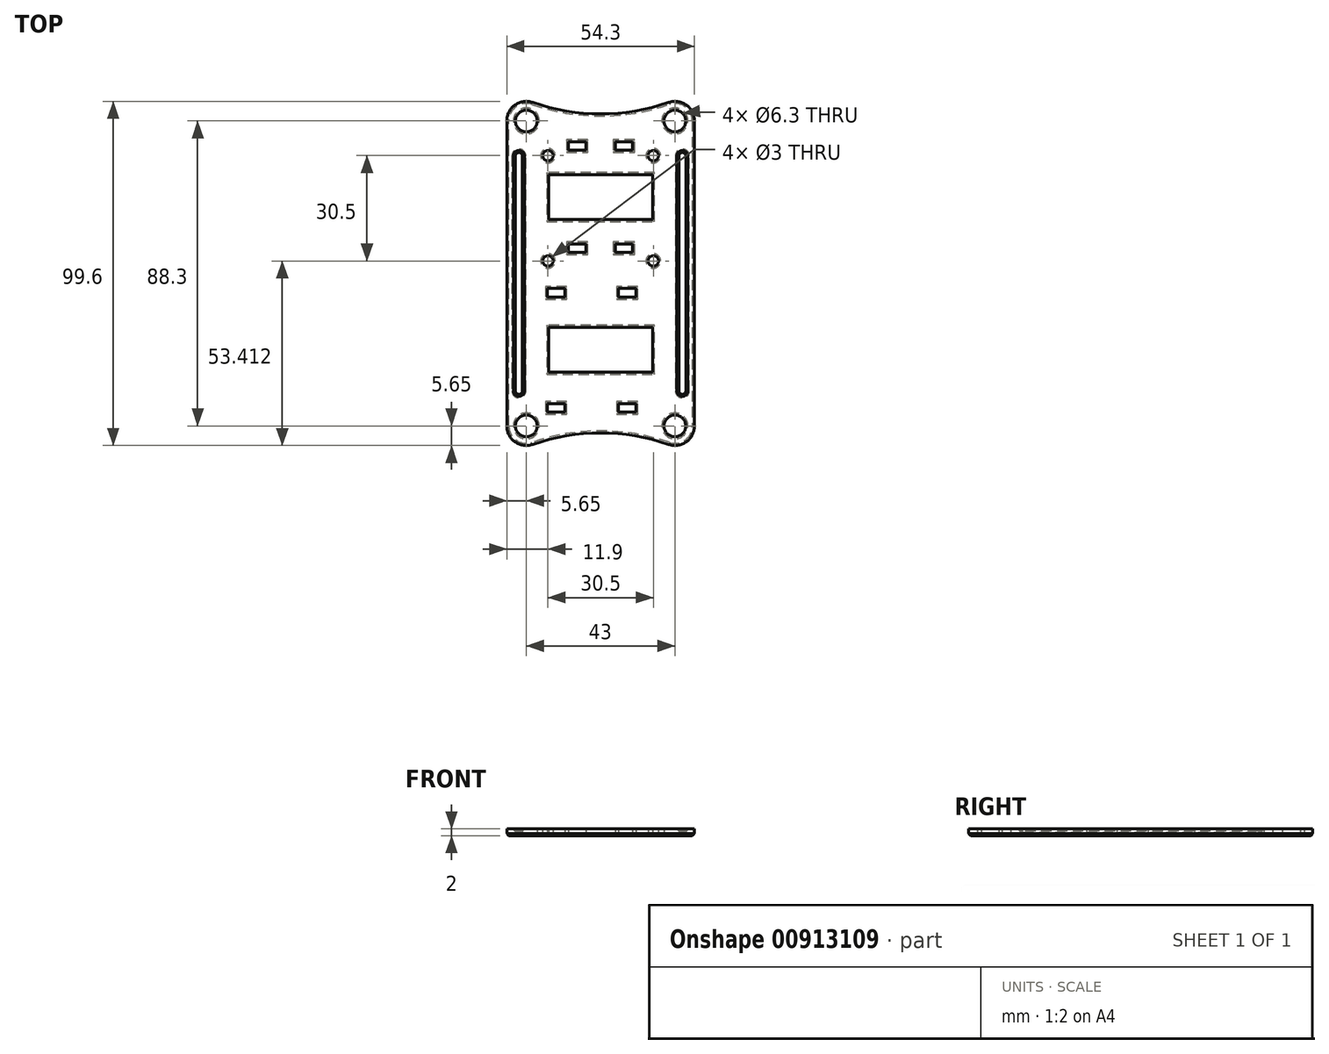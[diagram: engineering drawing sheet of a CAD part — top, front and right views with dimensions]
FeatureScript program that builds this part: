
annotation { "Feature Type Name" : "Feature", "Feature Type Description" : "" }
export const myFeature = defineFeature(function(context is Context, id is Id, definition is map)
    precondition{}
    {
        {
            var Q0;
            Q0=qCreatedBy(makeId("Top.planeOp"),FACE);
            var sketch = newSketch(context, id + "F0", { "sketchPlane" : qUnion([Q0])});
            skCircle(sketch, "E0", {"center": v(-21.5, 44.15) * mm, "radius": 3.15 * mm});
            skLineSegment(sketch, "E1", {"start": v(-21.5, 44.15) * mm, "end": v(21.5, 44.15) * mm, "construction": true});
            skCircle(sketch, "E2", {"center": v(21.5, 44.15) * mm, "radius": 3.15 * mm});
            skArc(sketch, "E3", {"start": v(-19.65, 49.49) * mm, "mid": v(-24.78, 48.75) * mm, "end": v(-27.15, 44.15) * mm});
            skLineSegment(sketch, "E4", {"start": v(0, 44.15) * mm, "end": v(0, -44.15) * mm, "construction": true});
            skArc(sketch, "E5.MirrorC", {"start": v(19.65, 49.49) * mm, "mid": v(24.78, 48.75) * mm, "end": v(27.15, 44.15) * mm});
            skArc(sketch, "E6", {"start": v(-19.65, 49.49) * mm, "mid": v(0, 46.18) * mm, "end": v(19.65, 49.49) * mm});
            skCircle(sketch, "E7", {"center": v(-21.5, -44.15) * mm, "radius": 3.15 * mm});
            skArc(sketch, "E8", {"start": v(-27.15, -44.15) * mm, "mid": v(-24.78, -48.75) * mm, "end": v(-19.65, -49.49) * mm});
            skLineSegment(sketch, "E9", {"start": v(-27.15, 44.15) * mm, "end": v(-27.15, -44.15) * mm});
            skLineSegment(sketch, "E10", {"start": v(0, 0) * mm, "end": v(21.5, 0) * mm, "construction": true});
            skArc(sketch, "E11.MirrorCS", {"start": v(-19.65, -49.49) * mm, "mid": v(0, -46.18) * mm, "end": v(19.65, -49.49) * mm});
            skArc(sketch, "E12", {"start": v(19.65, -49.49) * mm, "mid": v(24.78, -48.75) * mm, "end": v(27.15, -44.15) * mm});
            skCircle(sketch, "E13", {"center": v(21.5, -44.15) * mm, "radius": 3.15 * mm});
            skLineSegment(sketch, "E14.MirrorCS", {"start": v(27.15, 44.15) * mm, "end": v(27.15, -44.15) * mm});
            skCircle(sketch, "E15", {"center": v(-15.25, 34.11) * mm, "radius": 1.5 * mm});
            skCircle(sketch, "E16", {"center": v(15.25, 34.11) * mm, "radius": 1.5 * mm});
            skCircle(sketch, "E17", {"center": v(15.25, 3.61) * mm, "radius": 1.5 * mm});
            skCircle(sketch, "E18", {"center": v(-15.25, 3.61) * mm, "radius": 1.5 * mm});
            skLineSegment(sketch, "E19", {"start": v(-15.25, 34.11) * mm, "end": v(15.25, 34.11) * mm, "construction": true});
            skPoint(sketch, "E20", {"position": v(0, 34.11) * mm});
            skLineSegment(sketch, "E21", {"start": v(-25.61, -8.76) * mm, "end": v(20.39, -8.76) * mm, "construction": true});
            skLineSegment(sketch, "E22", {"start": v(20.39, -8.76) * mm, "end": v(20.39, -35.76) * mm, "construction": true});
            skLineSegment(sketch, "E23", {"start": v(20.39, -35.76) * mm, "end": v(-25.61, -35.76) * mm, "construction": true});
            skLineSegment(sketch, "E24", {"start": v(-25.61, -35.76) * mm, "end": v(-25.61, -8.76) * mm, "construction": true});
            skLineSegment(sketch, "E25.bottom", {"start": v(-15.38, -4.35) * mm, "end": v(-10.38, -4.35) * mm});
            skLineSegment(sketch, "E25.top", {"start": v(-15.38, -6.85) * mm, "end": v(-10.38, -6.85) * mm});
            skLineSegment(sketch, "E25.left", {"start": v(-15.38, -4.35) * mm, "end": v(-15.38, -6.85) * mm});
            skLineSegment(sketch, "E25.right", {"start": v(-10.38, -4.35) * mm, "end": v(-10.38, -6.85) * mm});
            skLineSegment(sketch, "E26.bottom", {"start": v(5.19, -4.35) * mm, "end": v(10.19, -4.35) * mm});
            skLineSegment(sketch, "E26.top", {"start": v(5.19, -6.85) * mm, "end": v(10.19, -6.85) * mm});
            skLineSegment(sketch, "E26.left", {"start": v(5.19, -4.35) * mm, "end": v(5.19, -6.85) * mm});
            skLineSegment(sketch, "E26.right", {"start": v(10.19, -4.35) * mm, "end": v(10.19, -6.85) * mm});
            skLineSegment(sketch, "E27", {"start": v(-25.61, -22.26) * mm, "end": v(20.39, -22.26) * mm, "construction": true});
            skLineSegment(sketch, "E28.MirrorCS", {"start": v(10.19, -40.16) * mm, "end": v(10.19, -37.66) * mm});
            skLineSegment(sketch, "E29.MirrorCS", {"start": v(-15.38, -40.16) * mm, "end": v(-15.38, -37.66) * mm});
            skLineSegment(sketch, "E30.MirrorCS", {"start": v(5.19, -40.16) * mm, "end": v(5.19, -37.66) * mm});
            skLineSegment(sketch, "E31.MirrorCS", {"start": v(-10.38, -40.16) * mm, "end": v(-10.38, -37.66) * mm});
            skLineSegment(sketch, "E32.MirrorCS", {"start": v(5.19, -40.16) * mm, "end": v(10.19, -40.16) * mm});
            skLineSegment(sketch, "E33.MirrorCS", {"start": v(-15.38, -40.16) * mm, "end": v(-10.38, -40.16) * mm});
            skLineSegment(sketch, "E34.MirrorCS", {"start": v(5.19, -37.66) * mm, "end": v(10.19, -37.66) * mm});
            skLineSegment(sketch, "E35.MirrorCS", {"start": v(-15.38, -37.66) * mm, "end": v(-10.38, -37.66) * mm});
            skLineSegment(sketch, "E36.bottom", {"start": v(-9.28, 38.15) * mm, "end": v(-4.28, 38.15) * mm});
            skLineSegment(sketch, "E36.top", {"start": v(-9.28, 35.65) * mm, "end": v(-4.28, 35.65) * mm});
            skLineSegment(sketch, "E36.left", {"start": v(-9.28, 38.15) * mm, "end": v(-9.28, 35.65) * mm});
            skLineSegment(sketch, "E36.right", {"start": v(-4.28, 38.15) * mm, "end": v(-4.28, 35.65) * mm});
            skLineSegment(sketch, "E37.bottom", {"start": v(15, 28.6) * mm, "end": v(-15, 28.6) * mm});
            skLineSegment(sketch, "E37.top", {"start": v(15, 15.6) * mm, "end": v(-15, 15.6) * mm});
            skLineSegment(sketch, "E37.left", {"start": v(15, 28.6) * mm, "end": v(15, 15.6) * mm});
            skLineSegment(sketch, "E37.right", {"start": v(-15, 28.6) * mm, "end": v(-15, 15.6) * mm});
            skPoint(sketch, "E38", {"position": v(0, 28.6) * mm});
            skLineSegment(sketch, "E39.MirrorCS", {"start": v(15, -28.6) * mm, "end": v(-15, -28.6) * mm});
            skLineSegment(sketch, "E40.MirrorCS", {"start": v(15, -15.6) * mm, "end": v(-15, -15.6) * mm});
            skLineSegment(sketch, "E41.MirrorCS", {"start": v(15, -28.6) * mm, "end": v(15, -15.6) * mm});
            skPoint(sketch, "E42.MirrorP", {"position": v(0, -28.6) * mm});
            skPoint(sketch, "E43.MirrorP", {"position": v(0, -34.11) * mm});
            skLineSegment(sketch, "E44.MirrorCS", {"start": v(-15, -28.6) * mm, "end": v(-15, -15.6) * mm});
            skLineSegment(sketch, "E45.MirrorCS", {"start": v(4.28, 38.15) * mm, "end": v(4.28, 35.65) * mm});
            skLineSegment(sketch, "E46.MirrorCS", {"start": v(9.28, 38.15) * mm, "end": v(4.28, 38.15) * mm});
            skLineSegment(sketch, "E47.MirrorCS", {"start": v(9.28, 38.15) * mm, "end": v(9.28, 35.65) * mm});
            skLineSegment(sketch, "E48.MirrorCS", {"start": v(9.28, 35.65) * mm, "end": v(4.28, 35.65) * mm});
            skLineSegment(sketch, "E49", {"start": v(-15, 22.1) * mm, "end": v(15, 22.1) * mm, "construction": true});
            skLineSegment(sketch, "E50.MirrorCS", {"start": v(-9.28, 8.57) * mm, "end": v(-4.28, 8.57) * mm});
            skLineSegment(sketch, "E51.MirrorCS", {"start": v(9.28, 6.07) * mm, "end": v(4.28, 6.07) * mm});
            skLineSegment(sketch, "E52.MirrorCS", {"start": v(9.28, 6.07) * mm, "end": v(9.28, 8.57) * mm});
            skLineSegment(sketch, "E53.MirrorCS", {"start": v(-9.28, 6.07) * mm, "end": v(-9.28, 8.57) * mm});
            skLineSegment(sketch, "E54.MirrorCS", {"start": v(-9.28, 6.07) * mm, "end": v(-4.28, 6.07) * mm});
            skLineSegment(sketch, "E55.MirrorCS", {"start": v(9.28, 8.57) * mm, "end": v(4.28, 8.57) * mm});
            skLineSegment(sketch, "E56.MirrorCS", {"start": v(4.28, 6.07) * mm, "end": v(4.28, 8.57) * mm});
            skLineSegment(sketch, "E57.MirrorCS", {"start": v(-4.28, 6.07) * mm, "end": v(-4.28, 8.57) * mm});
            skLineSegment(sketch, "E58.bottom", {"start": v(23.65, 35) * mm, "end": v(23.65, 35) * mm});
            skLineSegment(sketch, "E58.top", {"start": v(23.65, -35) * mm, "end": v(23.65, -35) * mm});
            skLineSegment(sketch, "E58.left", {"start": v(22.65, 34) * mm, "end": v(22.65, -34) * mm});
            skLineSegment(sketch, "E58.right", {"start": v(24.65, 34) * mm, "end": v(24.65, -34) * mm});
            skPoint(sketch, "E59.visualSharp", {"position": v(22.65, -35) * mm});
            skArc(sketch, "E59.filletArc", {"start": v(22.65, -34) * mm, "mid": v(22.94, -34.7) * mm, "end": v(23.65, -35) * mm});
            skPoint(sketch, "E60.visualSharp", {"position": v(24.65, -35) * mm});
            skArc(sketch, "E60.filletArc", {"start": v(23.65, -35) * mm, "mid": v(24.36, -34.7) * mm, "end": v(24.65, -34) * mm});
            skPoint(sketch, "E61.visualSharp", {"position": v(24.65, 35) * mm});
            skArc(sketch, "E61.filletArc", {"start": v(24.65, 34) * mm, "mid": v(24.36, 34.7) * mm, "end": v(23.65, 35) * mm});
            skPoint(sketch, "E62.visualSharp", {"position": v(22.65, 35) * mm});
            skArc(sketch, "E62.filletArc", {"start": v(23.65, 35) * mm, "mid": v(22.94, 34.7) * mm, "end": v(22.65, 34) * mm});
            skPoint(sketch, "E63", {"position": v(22.65, 0) * mm});
            skArc(sketch, "E64.MirrorCS", {"start": v(-23.65, -35) * mm, "mid": v(-24.36, -34.7) * mm, "end": v(-24.65, -34) * mm});
            skArc(sketch, "E65.MirrorCS", {"start": v(-24.65, 34) * mm, "mid": v(-24.36, 34.7) * mm, "end": v(-23.65, 35) * mm});
            skArc(sketch, "E66.MirrorCS", {"start": v(-22.65, -34) * mm, "mid": v(-22.94, -34.7) * mm, "end": v(-23.65, -35) * mm});
            skArc(sketch, "E67.MirrorCS", {"start": v(-23.65, 35) * mm, "mid": v(-22.94, 34.7) * mm, "end": v(-22.65, 34) * mm});
            skPoint(sketch, "E68.MirrorP", {"position": v(-22.65, -35) * mm});
            skPoint(sketch, "E69.MirrorP", {"position": v(-22.65, 35) * mm});
            skLineSegment(sketch, "E70.MirrorCS", {"start": v(-23.65, -35) * mm, "end": v(-23.65, -35) * mm});
            skPoint(sketch, "E71.MirrorP", {"position": v(-24.65, -35) * mm});
            skLineSegment(sketch, "E72.MirrorCS", {"start": v(-23.65, 35) * mm, "end": v(-23.65, 35) * mm});
            skLineSegment(sketch, "E73.MirrorCS", {"start": v(-24.65, 34) * mm, "end": v(-24.65, -34) * mm});
            skLineSegment(sketch, "E74.MirrorCS", {"start": v(-22.65, 34) * mm, "end": v(-22.65, -34) * mm});
            skPoint(sketch, "E75.MirrorP", {"position": v(-22.65, 0) * mm});
            skPoint(sketch, "E76.MirrorP", {"position": v(-24.65, 35) * mm});
            skSolve(sketch);
        }
        {
            var Q0;
            Q0=makeQuery(id+"F0.imprint","IMPRINT",FACE,{"disambiguationData":[TD([[makeQuery(id+"F0.imprint","IMPRINT",EDGE,{"derivedFrom":sQuery(id+"F0.wireOp",EDGE,"E0")}),-1.0]])]});
            extrude(context, id + "F1", {"entities" : qUnion([Q0]), "depth" : 2 * mm, "offsetDistance" : 25 * mm});
        }
        {
            var Q0;
            Q0=makeQuery(id+"F1.opExtrude","CAP_EDGE",EDGE,{"disambiguationData":[OSD([sQuery(id+"F0.wireOp",EDGE,"E14.MirrorCS")])],"isStart":true});
            var Q1;
            Q1=makeQuery(id+"F1.opExtrude","CAP_EDGE",EDGE,{"disambiguationData":[OSD([sQuery(id+"F0.wireOp",EDGE,"E13")])],"isStart":true});
            var Q2;
            Q2=makeQuery(id+"F1.opExtrude","CAP_EDGE",EDGE,{"disambiguationData":[OSD([sQuery(id+"F0.wireOp",EDGE,"E7")])],"isStart":true});
            var Q3;
            Q3=makeQuery(id+"F1.opExtrude","CAP_EDGE",EDGE,{"disambiguationData":[OSD([sQuery(id+"F0.wireOp",EDGE,"E29.MirrorCS")])],"isStart":true});
            var Q4;
            Q4=makeQuery(id+"F1.opExtrude","CAP_EDGE",EDGE,{"disambiguationData":[OSD([sQuery(id+"F0.wireOp",EDGE,"E35.MirrorCS")])],"isStart":true});
            var Q5;
            Q5=makeQuery(id+"F1.opExtrude","CAP_EDGE",EDGE,{"disambiguationData":[OSD([sQuery(id+"F0.wireOp",EDGE,"E31.MirrorCS")])],"isStart":true});
            var Q6;
            Q6=makeQuery(id+"F1.opExtrude","CAP_EDGE",EDGE,{"disambiguationData":[OSD([sQuery(id+"F0.wireOp",EDGE,"E33.MirrorCS")])],"isStart":true});
            var Q7;
            Q7=makeQuery(id+"F1.opExtrude","CAP_EDGE",EDGE,{"disambiguationData":[OSD([sQuery(id+"F0.wireOp",EDGE,"E30.MirrorCS")])],"isStart":true});
            var Q8;
            Q8=makeQuery(id+"F1.opExtrude","CAP_EDGE",EDGE,{"disambiguationData":[OSD([sQuery(id+"F0.wireOp",EDGE,"E34.MirrorCS")])],"isStart":true});
            var Q9;
            Q9=makeQuery(id+"F1.opExtrude","CAP_EDGE",EDGE,{"disambiguationData":[OSD([sQuery(id+"F0.wireOp",EDGE,"E28.MirrorCS")])],"isStart":true});
            var Q10;
            Q10=makeQuery(id+"F1.opExtrude","CAP_EDGE",EDGE,{"disambiguationData":[OSD([sQuery(id+"F0.wireOp",EDGE,"E32.MirrorCS")])],"isStart":true});
            var Q11;
            Q11=makeQuery(id+"F1.opExtrude","CAP_EDGE",EDGE,{"disambiguationData":[OSD([sQuery(id+"F0.wireOp",EDGE,"E39.MirrorCS")])],"isStart":true});
            var Q12;
            Q12=makeQuery(id+"F1.opExtrude","CAP_EDGE",EDGE,{"disambiguationData":[OSD([sQuery(id+"F0.wireOp",EDGE,"E41.MirrorCS")])],"isStart":true});
            var Q13;
            Q13=makeQuery(id+"F1.opExtrude","CAP_EDGE",EDGE,{"disambiguationData":[OSD([sQuery(id+"F0.wireOp",EDGE,"E40.MirrorCS")])],"isStart":true});
            var Q14;
            Q14=makeQuery(id+"F1.opExtrude","CAP_EDGE",EDGE,{"disambiguationData":[OSD([sQuery(id+"F0.wireOp",EDGE,"E44.MirrorCS")])],"isStart":true});
            var Q15;
            Q15=makeQuery(id+"F1.opExtrude","CAP_EDGE",EDGE,{"disambiguationData":[OSD([sQuery(id+"F0.wireOp",EDGE,"E25.left")])],"isStart":true});
            var Q16;
            Q16=makeQuery(id+"F1.opExtrude","CAP_EDGE",EDGE,{"disambiguationData":[OSD([sQuery(id+"F0.wireOp",EDGE,"E25.top")])],"isStart":true});
            var Q17;
            Q17=makeQuery(id+"F1.opExtrude","CAP_EDGE",EDGE,{"disambiguationData":[OSD([sQuery(id+"F0.wireOp",EDGE,"E25.right")])],"isStart":true});
            var Q18;
            Q18=makeQuery(id+"F1.opExtrude","CAP_EDGE",EDGE,{"disambiguationData":[OSD([sQuery(id+"F0.wireOp",EDGE,"E25.bottom")])],"isStart":true});
            var Q19;
            Q19=makeQuery(id+"F1.opExtrude","CAP_EDGE",EDGE,{"disambiguationData":[OSD([sQuery(id+"F0.wireOp",EDGE,"E26.left")])],"isStart":true});
            var Q20;
            Q20=makeQuery(id+"F1.opExtrude","CAP_EDGE",EDGE,{"disambiguationData":[OSD([sQuery(id+"F0.wireOp",EDGE,"E26.bottom")])],"isStart":true});
            var Q21;
            Q21=makeQuery(id+"F1.opExtrude","CAP_EDGE",EDGE,{"disambiguationData":[OSD([sQuery(id+"F0.wireOp",EDGE,"E26.top")])],"isStart":true});
            var Q22;
            Q22=makeQuery(id+"F1.opExtrude","CAP_EDGE",EDGE,{"disambiguationData":[OSD([sQuery(id+"F0.wireOp",EDGE,"E26.right")])],"isStart":true});
            var Q23;
            Q23=makeQuery(id+"F1.opExtrude","CAP_EDGE",EDGE,{"disambiguationData":[OSD([sQuery(id+"F0.wireOp",EDGE,"E17")])],"isStart":true});
            var Q24;
            Q24=makeQuery(id+"F1.opExtrude","CAP_EDGE",EDGE,{"disambiguationData":[OSD([sQuery(id+"F0.wireOp",EDGE,"E18")])],"isStart":true});
            var Q25;
            Q25=makeQuery(id+"F1.opExtrude","CAP_EDGE",EDGE,{"disambiguationData":[OSD([sQuery(id+"F0.wireOp",EDGE,"E52.MirrorCS")])],"isStart":true});
            var Q26;
            Q26=makeQuery(id+"F1.opExtrude","CAP_EDGE",EDGE,{"disambiguationData":[OSD([sQuery(id+"F0.wireOp",EDGE,"E55.MirrorCS")])],"isStart":true});
            var Q27;
            Q27=makeQuery(id+"F1.opExtrude","CAP_EDGE",EDGE,{"disambiguationData":[OSD([sQuery(id+"F0.wireOp",EDGE,"E51.MirrorCS")])],"isStart":true});
            var Q28;
            Q28=makeQuery(id+"F1.opExtrude","CAP_EDGE",EDGE,{"disambiguationData":[OSD([sQuery(id+"F0.wireOp",EDGE,"E56.MirrorCS")])],"isStart":true});
            var Q29;
            Q29=makeQuery(id+"F1.opExtrude","CAP_EDGE",EDGE,{"disambiguationData":[OSD([sQuery(id+"F0.wireOp",EDGE,"E57.MirrorCS")])],"isStart":true});
            var Q30;
            Q30=makeQuery(id+"F1.opExtrude","CAP_EDGE",EDGE,{"disambiguationData":[OSD([sQuery(id+"F0.wireOp",EDGE,"E50.MirrorCS")])],"isStart":true});
            var Q31;
            Q31=makeQuery(id+"F1.opExtrude","CAP_EDGE",EDGE,{"disambiguationData":[OSD([sQuery(id+"F0.wireOp",EDGE,"E54.MirrorCS")])],"isStart":true});
            var Q32;
            Q32=makeQuery(id+"F1.opExtrude","CAP_EDGE",EDGE,{"disambiguationData":[OSD([sQuery(id+"F0.wireOp",EDGE,"E53.MirrorCS")])],"isStart":true});
            var Q33;
            Q33=makeQuery(id+"F1.opExtrude","CAP_EDGE",EDGE,{"disambiguationData":[OSD([sQuery(id+"F0.wireOp",EDGE,"E37.top")])],"isStart":true});
            var Q34;
            Q34=makeQuery(id+"F1.opExtrude","CAP_EDGE",EDGE,{"disambiguationData":[OSD([sQuery(id+"F0.wireOp",EDGE,"E37.left")])],"isStart":true});
            var Q35;
            Q35=makeQuery(id+"F1.opExtrude","CAP_EDGE",EDGE,{"disambiguationData":[OSD([sQuery(id+"F0.wireOp",EDGE,"E37.bottom")])],"isStart":true});
            var Q36;
            Q36=makeQuery(id+"F1.opExtrude","CAP_EDGE",EDGE,{"disambiguationData":[OSD([sQuery(id+"F0.wireOp",EDGE,"E37.right")])],"isStart":true});
            var Q37;
            Q37=makeQuery(id+"F1.opExtrude","CAP_EDGE",EDGE,{"disambiguationData":[OSD([sQuery(id+"F0.wireOp",EDGE,"E16")])],"isStart":true});
            var Q38;
            Q38=makeQuery(id+"F1.opExtrude","CAP_EDGE",EDGE,{"disambiguationData":[OSD([sQuery(id+"F0.wireOp",EDGE,"E47.MirrorCS")])],"isStart":true});
            var Q39;
            Q39=makeQuery(id+"F1.opExtrude","CAP_EDGE",EDGE,{"disambiguationData":[OSD([sQuery(id+"F0.wireOp",EDGE,"E48.MirrorCS")])],"isStart":true});
            var Q40;
            Q40=makeQuery(id+"F1.opExtrude","CAP_EDGE",EDGE,{"disambiguationData":[OSD([sQuery(id+"F0.wireOp",EDGE,"E46.MirrorCS")])],"isStart":true});
            var Q41;
            Q41=makeQuery(id+"F1.opExtrude","CAP_EDGE",EDGE,{"disambiguationData":[OSD([sQuery(id+"F0.wireOp",EDGE,"E45.MirrorCS")])],"isStart":true});
            var Q42;
            Q42=makeQuery(id+"F1.opExtrude","CAP_EDGE",EDGE,{"disambiguationData":[OSD([sQuery(id+"F0.wireOp",EDGE,"E36.right")])],"isStart":true});
            var Q43;
            Q43=makeQuery(id+"F1.opExtrude","CAP_EDGE",EDGE,{"disambiguationData":[OSD([sQuery(id+"F0.wireOp",EDGE,"E36.bottom")])],"isStart":true});
            var Q44;
            Q44=makeQuery(id+"F1.opExtrude","CAP_EDGE",EDGE,{"disambiguationData":[OSD([sQuery(id+"F0.wireOp",EDGE,"E36.top")])],"isStart":true});
            var Q45;
            Q45=makeQuery(id+"F1.opExtrude","CAP_EDGE",EDGE,{"disambiguationData":[OSD([sQuery(id+"F0.wireOp",EDGE,"E36.left")])],"isStart":true});
            var Q46;
            Q46=makeQuery(id+"F1.opExtrude","CAP_EDGE",EDGE,{"disambiguationData":[OSD([sQuery(id+"F0.wireOp",EDGE,"E2")])],"isStart":true});
            var Q47;
            Q47=makeQuery(id+"F1.opExtrude","CAP_EDGE",EDGE,{"disambiguationData":[OSD([sQuery(id+"F0.wireOp",EDGE,"E0")])],"isStart":true});
            var Q48;
            Q48=makeQuery(id+"F1.opExtrude","CAP_EDGE",EDGE,{"disambiguationData":[OSD([sQuery(id+"F0.wireOp",EDGE,"E15")])],"isStart":true});
            var Q49;
            Q49=makeQuery(id+"F1.opExtrude","CAP_EDGE",EDGE,{"disambiguationData":[OSD([sQuery(id+"F0.wireOp",EDGE,"E58.left")])],"isStart":false});
            var Q50;
            Q50=makeQuery(id+"F1.opExtrude","CAP_EDGE",EDGE,{"disambiguationData":[OSD([sQuery(id+"F0.wireOp",EDGE,"E74.MirrorCS")])],"isStart":false});
            chamfer(context, id + "F2", {"entities" : qUnion([Q0, Q1, Q2, Q3, Q4, Q5, Q6, Q7, Q8, Q9, Q10, Q11, Q12, Q13, Q14, Q15, Q16, Q17, Q18, Q19, Q20, Q21, Q22, Q23, Q24, Q25, Q26, Q27, Q28, Q29, Q30, Q31, Q32, Q33, Q34, Q35, Q36, Q37, Q38, Q39, Q40, Q41, Q42, Q43, Q44, Q45, Q46, Q47, Q48, Q49, Q50]), "width" : 0.6 * mm, "tangentPropagation" : true});
        }
        {
            var Q0;
            Q0=makeQuery(id+"F1.opExtrude","CAP_EDGE",EDGE,{"disambiguationData":[OSD([sQuery(id+"F0.wireOp",EDGE,"E58.left")])],"isStart":true});
            var Q1;
            Q1=makeQuery(id+"F1.opExtrude","CAP_EDGE",EDGE,{"disambiguationData":[OSD([sQuery(id+"F0.wireOp",EDGE,"E74.MirrorCS")])],"isStart":true});
            chamfer(context, id + "F3", {"entities" : qUnion([Q0, Q1]), "width" : 1 * mm, "tangentPropagation" : true});
        }
    });
